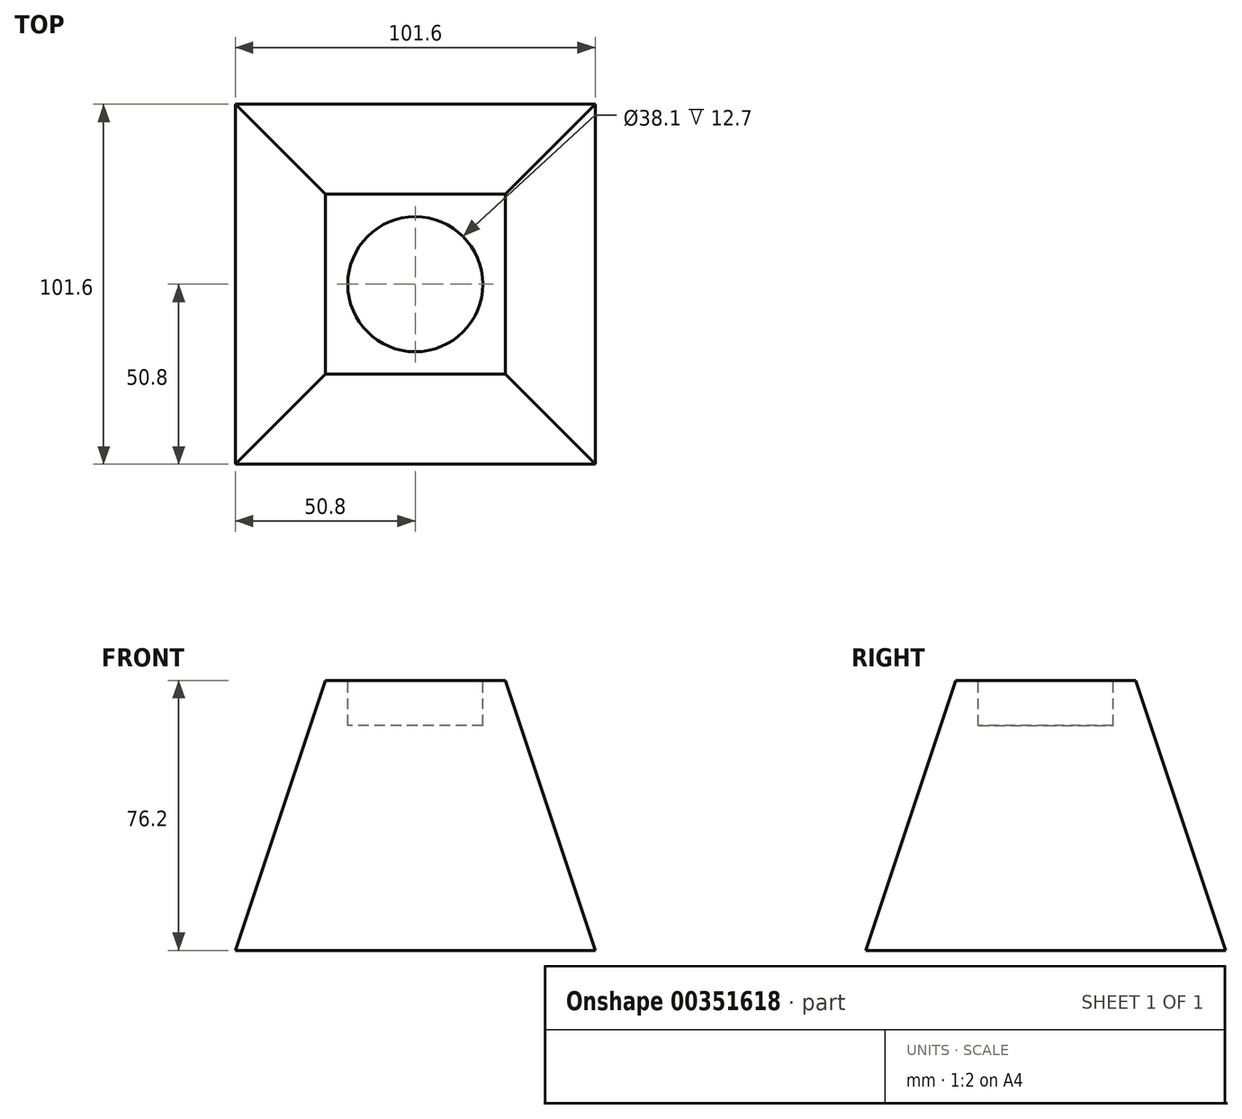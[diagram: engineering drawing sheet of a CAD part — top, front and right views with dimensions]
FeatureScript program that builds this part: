
annotation { "Feature Type Name" : "Feature", "Feature Type Description" : "" }
export const myFeature = defineFeature(function(context is Context, id is Id, definition is map)
    precondition{}
    {
        {
            var Q0;
            Q0=qCreatedBy(makeId("Top.planeOp"),FACE);
            var sketch = newSketch(context, id + "F0", { "sketchPlane" : qUnion([Q0])});
            skLineSegment(sketch, "E0.bottom", {"start": v(50.8, -50.8) * mm, "end": v(-50.8, -50.8) * mm});
            skLineSegment(sketch, "E0.top", {"start": v(50.8, 50.8) * mm, "end": v(-50.8, 50.8) * mm});
            skLineSegment(sketch, "E0.left", {"start": v(50.8, -50.8) * mm, "end": v(50.8, 50.8) * mm});
            skLineSegment(sketch, "E0.right", {"start": v(-50.8, -50.8) * mm, "end": v(-50.8, 50.8) * mm});
            skPoint(sketch, "E0.middle", {"position": v(0, 0) * mm});
            skSolve(sketch);
        }
        {
            var Q0;
            Q0=qCreatedBy(makeId("Top.planeOp"),FACE);
            cPlane(context, id + "F1", {"entities" : qUnion([Q0]), "cplaneType" : CPlaneType.OFFSET, "offset" : 76.2 * mm, "width" : 152.4 * mm, "height" : 152.4 * mm});
        }
        {
            var Q0;
            Q0=qCreatedBy(id+"F1.planeOp",FACE);
            var sketch = newSketch(context, id + "F2", { "sketchPlane" : qUnion([Q0])});
            skLineSegment(sketch, "E1.bottom", {"start": v(25.4, 25.4) * mm, "end": v(-25.4, 25.4) * mm});
            skLineSegment(sketch, "E1.top", {"start": v(25.4, -25.4) * mm, "end": v(-25.4, -25.4) * mm});
            skLineSegment(sketch, "E1.left", {"start": v(25.4, 25.4) * mm, "end": v(25.4, -25.4) * mm});
            skLineSegment(sketch, "E1.right", {"start": v(-25.4, 25.4) * mm, "end": v(-25.4, -25.4) * mm});
            skPoint(sketch, "E1.middle", {"position": v(0, 0) * mm});
            skSolve(sketch);
        }
        {
            var Q0;
            Q0=makeQuery(id+"F2.imprint","IMPRINT",FACE,{"disambiguationData":[TD([[makeQuery(id+"F2.imprint","IMPRINT",EDGE,{"derivedFrom":sQuery(id+"F2.wireOp",EDGE,"E1.bottom")}),1.0]])]});
            var Q1;
            Q1=makeQuery(id+"F0.imprint","IMPRINT",FACE,{"disambiguationData":[TD([[makeQuery(id+"F0.imprint","IMPRINT",EDGE,{"derivedFrom":sQuery(id+"F0.wireOp",EDGE,"E0.bottom")}),-1.0]])]});
            loft(context, id + "F3", {"sheetProfilesArray" : [{ "sheetProfileEntities" : qUnion([Q0]) }, { "sheetProfileEntities" : qUnion([Q1]) }]});
        }
        {
            var Q0;
            Q0=makeQuery(id+"F3.opLoft","CAP_FACE",FACE,{"disambiguationData":[OSD([makeQuery(id+"F2.imprint","IMPRINT",FACE,{"disambiguationData":[TD([[makeQuery(id+"F2.imprint","IMPRINT",EDGE,{"derivedFrom":sQuery(id+"F2.wireOp",EDGE,"E1.bottom")}),1.0]])]})])],"isStart":true});
            var sketch = newSketch(context, id + "F4", { "sketchPlane" : qUnion([Q0])});
            skCircle(sketch, "E2", {"center": v(0, 0) * mm, "radius": 19.05 * mm});
            skSolve(sketch);
        }
        {
            var Q0;
            Q0=makeQuery(id+"F4.imprint","IMPRINT",FACE,{"disambiguationData":[TD([[makeQuery(id+"F4.imprint","IMPRINT",EDGE,{"derivedFrom":sQuery(id+"F4.wireOp",EDGE,"E2")}),1.0]])]});
            var Q1;
            Q1=sQuery(id+"F4.wireOp",EDGE,"E2");
            extrude(context, id + "F5", {"entities" : qUnion([Q0]), "operationType" : NewBodyOperationType.REMOVE, "surfaceEntities" : qUnion([Q1]), "oppositeDirection" : true, "depth" : 12.7 * mm});
        }
    });
